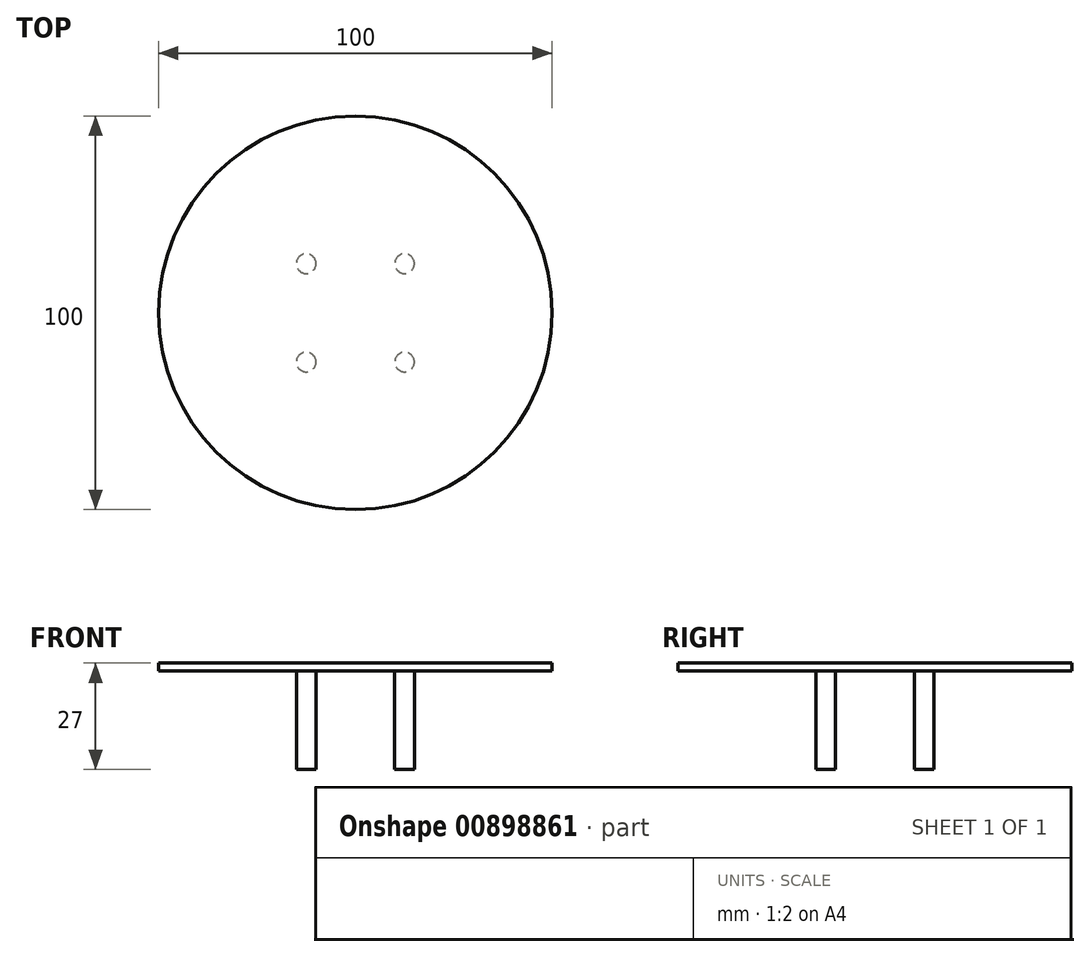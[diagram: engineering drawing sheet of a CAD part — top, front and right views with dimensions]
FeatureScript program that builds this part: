
annotation { "Feature Type Name" : "Feature", "Feature Type Description" : "" }
export const myFeature = defineFeature(function(context is Context, id is Id, definition is map)
    precondition{}
    {
        {
            var Q0;
            Q0=qCreatedBy(makeId("Top.planeOp"),FACE);
            var sketch = newSketch(context, id + "F0", { "sketchPlane" : qUnion([Q0])});
            skLineSegment(sketch, "E0.bottom", {"start": v(12.5, -12.5) * mm, "end": v(-12.5, -12.5) * mm, "construction": true});
            skLineSegment(sketch, "E0.top", {"start": v(12.5, 12.5) * mm, "end": v(-12.5, 12.5) * mm, "construction": true});
            skLineSegment(sketch, "E0.left", {"start": v(12.5, -12.5) * mm, "end": v(12.5, 12.5) * mm, "construction": true});
            skLineSegment(sketch, "E0.right", {"start": v(-12.5, -12.5) * mm, "end": v(-12.5, 12.5) * mm, "construction": true});
            skPoint(sketch, "E0.middle", {"position": v(0, 0) * mm});
            skCircle(sketch, "E1", {"center": v(-12.5, 12.5) * mm, "radius": 2.5 * mm});
            skCircle(sketch, "E2.1.0", {"center": v(-12.5, -12.5) * mm, "radius": 2.5 * mm});
            skCircle(sketch, "E2.2.0", {"center": v(12.5, -12.5) * mm, "radius": 2.5 * mm});
            skCircle(sketch, "E2.3.0", {"center": v(12.5, 12.5) * mm, "radius": 2.5 * mm});
            skSolve(sketch);
        }
        {
            var Q0;
            Q0=makeQuery(id+"F0.imprint","IMPRINT",FACE,{"disambiguationData":[TD([[makeQuery(id+"F0.imprint","IMPRINT",EDGE,{"derivedFrom":sQuery(id+"F0.wireOp",EDGE,"E2.3.0")}),1.0]])]});
            var Q1;
            Q1=makeQuery(id+"F0.imprint","IMPRINT",FACE,{"disambiguationData":[TD([[makeQuery(id+"F0.imprint","IMPRINT",EDGE,{"derivedFrom":sQuery(id+"F0.wireOp",EDGE,"E2.1.0")}),1.0]])]});
            var Q2;
            Q2=makeQuery(id+"F0.imprint","IMPRINT",FACE,{"disambiguationData":[TD([[makeQuery(id+"F0.imprint","IMPRINT",EDGE,{"derivedFrom":sQuery(id+"F0.wireOp",EDGE,"E2.2.0")}),1.0]])]});
            var Q3;
            Q3=makeQuery(id+"F0.imprint","IMPRINT",FACE,{"disambiguationData":[TD([[makeQuery(id+"F0.imprint","IMPRINT",EDGE,{"derivedFrom":sQuery(id+"F0.wireOp",EDGE,"E1")}),1.0]])]});
            extrude(context, id + "F1", {"entities" : qUnion([Q0, Q1, Q2, Q3]), "depth" : 25 * mm, "offsetDistance" : 25 * mm});
        }
        {
            var Q0;
            Q0=makeQuery(id+"F1.opExtrude","CAP_FACE",FACE,{"disambiguationData":[OSD([sQuery(id+"F0.wireOp",EDGE,"E2.3.0")])],"isStart":false});
            var sketch = newSketch(context, id + "F2", { "sketchPlane" : qUnion([Q0])});
            skCircle(sketch, "E3", {"center": v(0, 0) * mm, "radius": 50 * mm});
            skSolve(sketch);
        }
        {
            var Q0;
            Q0=makeQuery(id+"F2.imprint","IMPRINT",FACE,{"disambiguationData":[TD([[makeQuery(id+"F2.imprint","IMPRINT",EDGE,{"derivedFrom":sQuery(id+"F2.wireOp",EDGE,"E3")}),1.0]])]});
            extrude(context, id + "F3", {"entities" : qUnion([Q0]), "depth" : 25 * mm, "offsetDistance" : 25 * mm});
        }
        {
            var Q0;
            Q0=makeQuery(id+"F3.opExtrude","SWEPT_BODY",BODY,{"disambiguationData":[OSD([sQuery(id+"F0.wireOp",EDGE,"E2.3.0"),sQuery(id+"F2.wireOp",EDGE,"E3")])]});
            deleteBodies(context, id + "F4", {"entities" : qUnion([Q0])});
        }
        {
            var Q0;
            Q0=makeQuery(id+"F1.opExtrude","CAP_FACE",FACE,{"disambiguationData":[OSD([sQuery(id+"F0.wireOp",EDGE,"E2.3.0")])],"isStart":false});
            var sketch = newSketch(context, id + "F5", { "sketchPlane" : qUnion([Q0])});
            skCircle(sketch, "E4", {"center": v(0, 0) * mm, "radius": 50 * mm});
            skSolve(sketch);
        }
        {
            var Q0;
            Q0=makeQuery(id+"F5.imprint","IMPRINT",FACE,{"disambiguationData":[TD([[makeQuery(id+"F5.imprint","IMPRINT",EDGE,{"derivedFrom":sQuery(id+"F5.wireOp",EDGE,"E4")}),1.0]])]});
            var Q1;
            Q1=makeQuery(id+"F5.imprint","IMPRINT",FACE,{"disambiguationData":[TD([[makeQuery(id+"F5.imprint","IMPRINT",EDGE,{"derivedFrom":makeQuery(id+"F1.opExtrude","CAP_EDGE",EDGE,{"disambiguationData":[OSD([sQuery(id+"F0.wireOp",EDGE,"E2.3.0")])],"isStart":false})}),1.0]])]});
            extrude(context, id + "F6", {"entities" : qUnion([Q0, Q1]), "operationType" : NewBodyOperationType.ADD, "depth" : 2 * mm, "offsetDistance" : 25 * mm});
        }
    });
